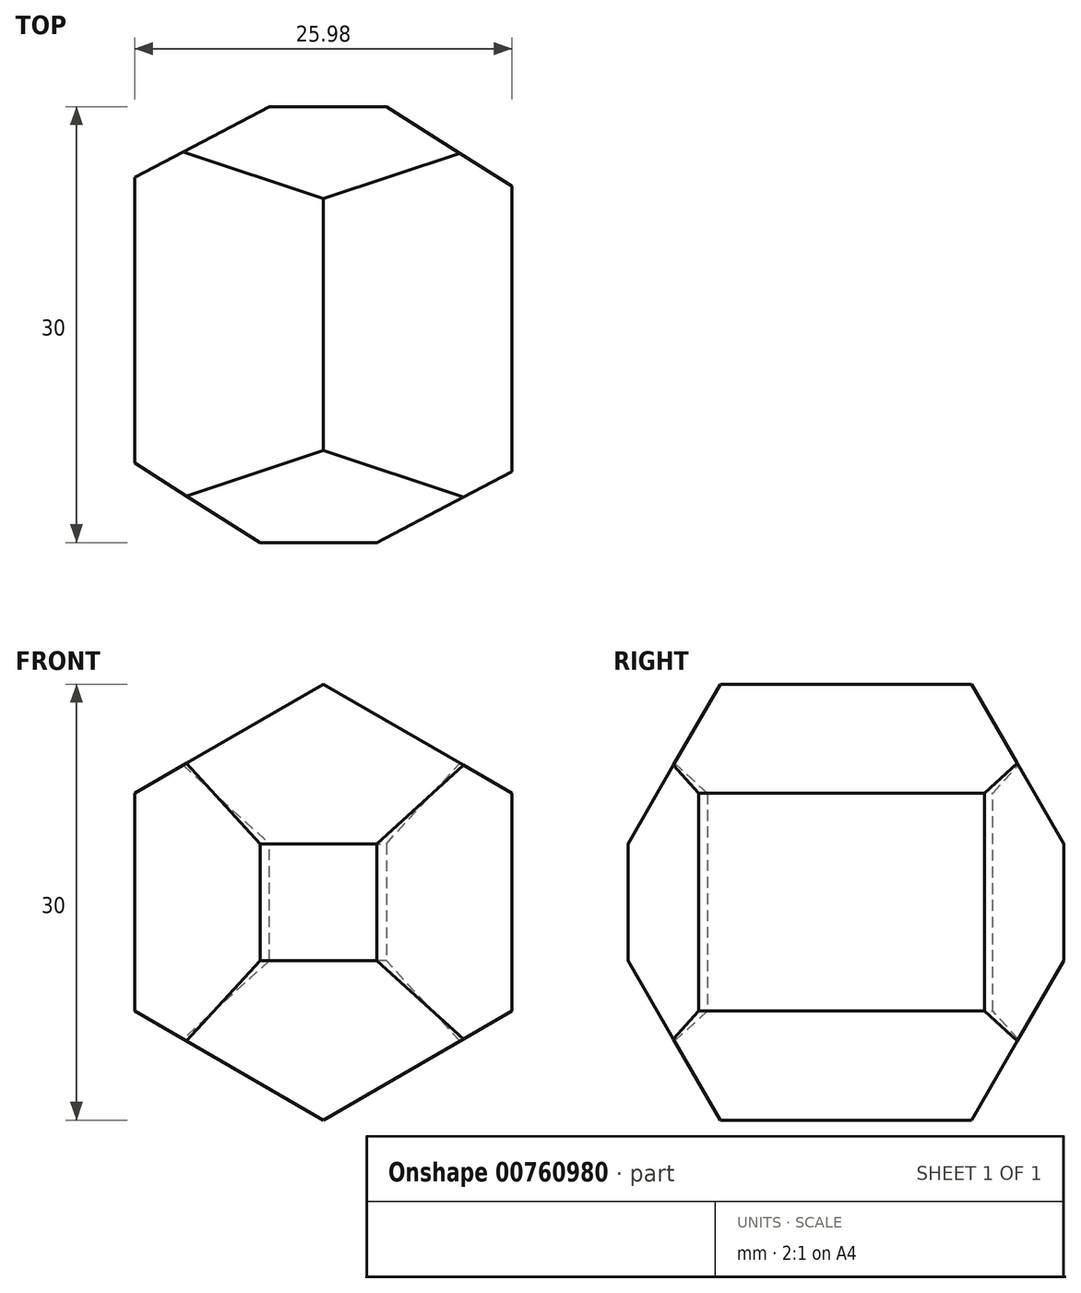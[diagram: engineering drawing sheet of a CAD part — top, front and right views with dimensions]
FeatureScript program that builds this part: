
annotation { "Feature Type Name" : "Feature", "Feature Type Description" : "" }
export const myFeature = defineFeature(function(context is Context, id is Id, definition is map)
    precondition{}
    {
        {
            var Q0;
            Q0=qCreatedBy(makeId("Top.planeOp"),FACE);
            var sketch = newSketch(context, id + "F0", { "sketchPlane" : qUnion([Q0])});
            skCircle(sketch, "E0.cCircle", {"center": v(0, 0) * mm, "radius": 15 * mm, "construction": true});
            skLineSegment(sketch, "E0.0", {"start": v(15.34, 8.05) * mm, "end": v(14.64, -9.26) * mm});
            skLineSegment(sketch, "E0.1", {"start": v(14.64, -9.26) * mm, "end": v(-0.7, -17.3) * mm});
            skLineSegment(sketch, "E0.2", {"start": v(-0.7, -17.3) * mm, "end": v(-15.34, -8.05) * mm});
            skLineSegment(sketch, "E0.3", {"start": v(-15.34, -8.05) * mm, "end": v(-14.64, 9.26) * mm});
            skLineSegment(sketch, "E0.4", {"start": v(-14.64, 9.26) * mm, "end": v(0.7, 17.3) * mm});
            skLineSegment(sketch, "E0.5", {"start": v(0.7, 17.3) * mm, "end": v(15.34, 8.05) * mm});
            skPoint(sketch, "E0.0.midPoint", {"position": v(14.99, -0.6) * mm});
            skLineSegment(sketch, "E1", {"start": v(0, 0) * mm, "end": v(-0.7, -17.3) * mm, "construction": true});
            skSolve(sketch);
        }
        {
            var Q0;
            Q0=qSketchRegion(id+"F0",true);
            extrude(context, id + "F1", {"entities" : qUnion([Q0]), "endBound" : BoundingType.SYMMETRIC, "depth" : 30 * mm});
        }
        {
            var Q0;
            Q0=qCreatedBy(makeId("Right.planeOp"),FACE);
            var sketch = newSketch(context, id + "F2", { "sketchPlane" : qUnion([Q0])});
            skCircle(sketch, "E2.cCircle", {"center": v(0, 0) * mm, "radius": 15 * mm, "construction": true});
            skLineSegment(sketch, "E2.0", {"start": v(-8.66, 15) * mm, "end": v(8.66, 15) * mm});
            skLineSegment(sketch, "E2.1", {"start": v(8.66, 15) * mm, "end": v(17.32, 0) * mm});
            skLineSegment(sketch, "E2.2", {"start": v(17.32, 0) * mm, "end": v(8.66, -15) * mm});
            skLineSegment(sketch, "E2.3", {"start": v(8.66, -15) * mm, "end": v(-8.66, -15) * mm});
            skLineSegment(sketch, "E2.4", {"start": v(-8.66, -15) * mm, "end": v(-17.32, 0) * mm});
            skLineSegment(sketch, "E2.5", {"start": v(-17.32, 0) * mm, "end": v(-8.66, 15) * mm});
            skPoint(sketch, "E2.0.midPoint", {"position": v(0, 15) * mm});
            skSolve(sketch);
        }
        {
            var Q0;
            Q0=qSketchRegion(id+"F2",true);
            extrude(context, id + "F3", {"entities" : qUnion([Q0]), "operationType" : NewBodyOperationType.INTERSECT, "endBound" : BoundingType.SYMMETRIC, "depth" : 30 * mm});
        }
        {
            var Q0;
            Q0=qCreatedBy(makeId("Front.planeOp"),FACE);
            var sketch = newSketch(context, id + "F4", { "sketchPlane" : qUnion([Q0])});
            skCircle(sketch, "E3.cCircle", {"center": v(0, 0) * mm, "radius": 13 * mm, "construction": true});
            skLineSegment(sketch, "E3.0", {"start": v(-13, -7.5) * mm, "end": v(-13, 7.5) * mm});
            skLineSegment(sketch, "E3.1", {"start": v(-13, 7.5) * mm, "end": v(0, 15) * mm});
            skLineSegment(sketch, "E3.2", {"start": v(0, 15) * mm, "end": v(13, 7.5) * mm});
            skLineSegment(sketch, "E3.3", {"start": v(13, 7.5) * mm, "end": v(13, -7.5) * mm});
            skLineSegment(sketch, "E3.4", {"start": v(13, -7.5) * mm, "end": v(0, -15) * mm});
            skLineSegment(sketch, "E3.5", {"start": v(0, -15) * mm, "end": v(-13, -7.5) * mm});
            skPoint(sketch, "E3.0.midPoint", {"position": v(-13, 0) * mm});
            skLineSegment(sketch, "E4", {"start": v(0, -15) * mm, "end": v(0, 0) * mm, "construction": true});
            skSolve(sketch);
        }
        {
            var Q0;
            Q0=qSketchRegion(id+"F4",true);
            extrude(context, id + "F5", {"entities" : qUnion([Q0]), "operationType" : NewBodyOperationType.INTERSECT, "endBound" : BoundingType.SYMMETRIC, "depth" : 30 * mm});
        }
    });
